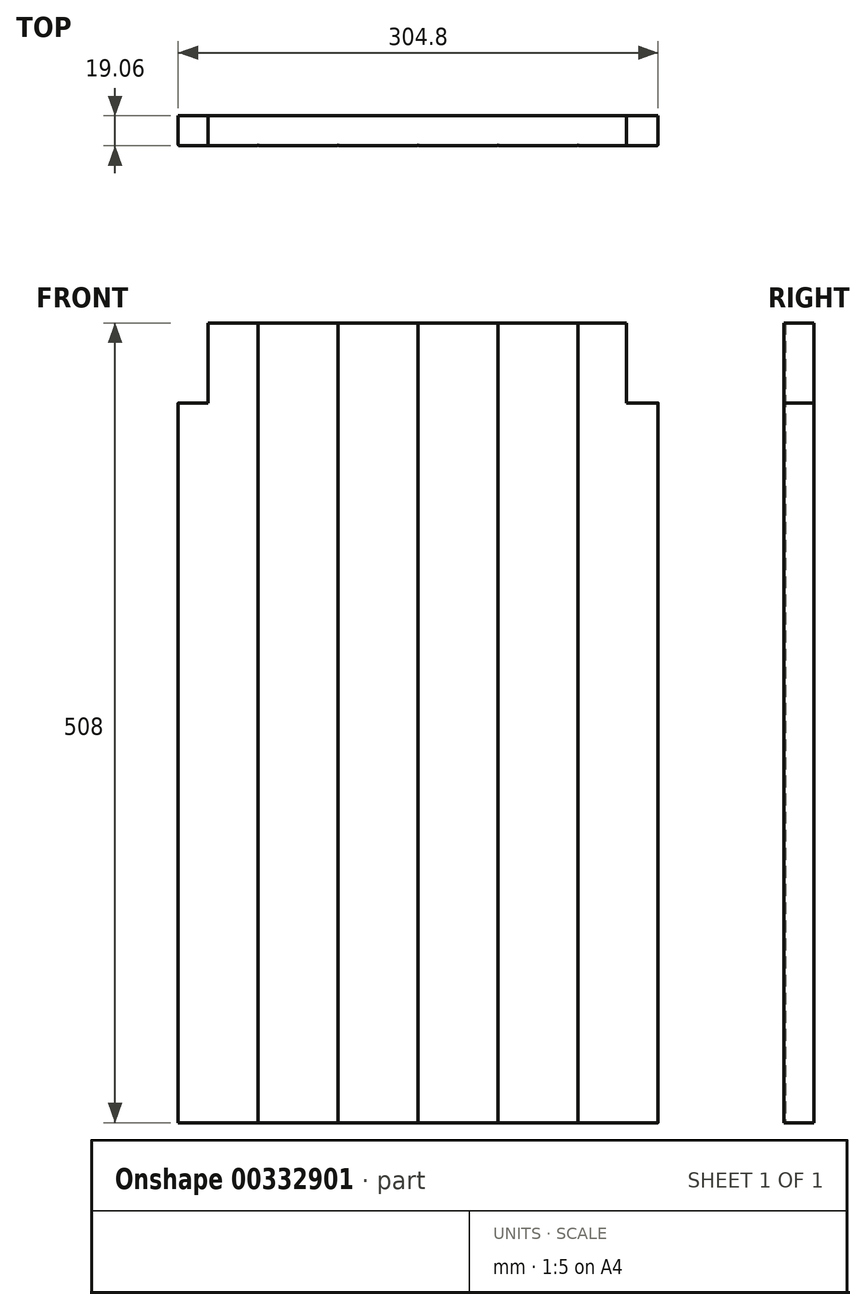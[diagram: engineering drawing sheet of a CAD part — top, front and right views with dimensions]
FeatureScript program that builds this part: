
annotation { "Feature Type Name" : "Feature", "Feature Type Description" : "" }
export const myFeature = defineFeature(function(context is Context, id is Id, definition is map)
    precondition{}
    {
        {
            var Q0;
            Q0=qCreatedBy(makeId("Top.planeOp"),FACE);
            var sketch = newSketch(context, id + "F0", { "sketchPlane" : qUnion([Q0])});
            skLineSegment(sketch, "E0.bottom", {"start": v(533.4, -9.53) * mm, "end": v(458.22, -9.53) * mm});
            skLineSegment(sketch, "E0.top", {"start": v(533.4, 9.53) * mm, "end": v(-533.4, 9.53) * mm});
            skLineSegment(sketch, "E0.left", {"start": v(533.4, 9.53) * mm, "end": v(533.4, -9.53) * mm});
            skLineSegment(sketch, "E0.right", {"start": v(-533.4, 9.53) * mm, "end": v(-533.4, -9.53) * mm});
            skPoint(sketch, "E0.middle", {"position": v(0, 0) * mm});
            skArc(sketch, "E1", {"start": v(-509.02, -9.53) * mm, "mid": v(-508.3, -9.23) * mm, "end": v(-508, -8.5) * mm});
            skArc(sketch, "E2", {"start": v(-508, -8.5) * mm, "mid": v(-507.7, -9.23) * mm, "end": v(-506.98, -9.52) * mm});
            skArc(sketch, "E3.1.0.0", {"start": v(-458.22, -9.53) * mm, "mid": v(-457.5, -9.23) * mm, "end": v(-457.2, -8.5) * mm});
            skArc(sketch, "E3.1.0.1", {"start": v(-457.2, -8.5) * mm, "mid": v(-456.9, -9.23) * mm, "end": v(-456.18, -9.52) * mm});
            skArc(sketch, "E3.2.0.0", {"start": v(-407.42, -9.53) * mm, "mid": v(-406.7, -9.23) * mm, "end": v(-406.4, -8.5) * mm});
            skArc(sketch, "E3.2.0.1", {"start": v(-406.4, -8.5) * mm, "mid": v(-406.1, -9.23) * mm, "end": v(-405.38, -9.52) * mm});
            skArc(sketch, "E3.3.0.0", {"start": v(-356.62, -9.53) * mm, "mid": v(-355.9, -9.23) * mm, "end": v(-355.6, -8.5) * mm});
            skArc(sketch, "E3.3.0.1", {"start": v(-355.6, -8.5) * mm, "mid": v(-355.3, -9.23) * mm, "end": v(-354.58, -9.52) * mm});
            skArc(sketch, "E3.4.0.0", {"start": v(-305.82, -9.53) * mm, "mid": v(-305.1, -9.23) * mm, "end": v(-304.8, -8.5) * mm});
            skArc(sketch, "E3.4.0.1", {"start": v(-304.8, -8.5) * mm, "mid": v(-304.5, -9.23) * mm, "end": v(-303.78, -9.52) * mm});
            skArc(sketch, "E3.5.0.0", {"start": v(-255.02, -9.53) * mm, "mid": v(-254.3, -9.23) * mm, "end": v(-254, -8.5) * mm});
            skArc(sketch, "E3.5.0.1", {"start": v(-254, -8.5) * mm, "mid": v(-253.7, -9.23) * mm, "end": v(-252.98, -9.52) * mm});
            skArc(sketch, "E3.6.0.0", {"start": v(-204.22, -9.53) * mm, "mid": v(-203.5, -9.23) * mm, "end": v(-203.2, -8.5) * mm});
            skArc(sketch, "E3.6.0.1", {"start": v(-203.2, -8.5) * mm, "mid": v(-202.9, -9.23) * mm, "end": v(-202.18, -9.52) * mm});
            skArc(sketch, "E3.7.0.0", {"start": v(-153.42, -9.53) * mm, "mid": v(-152.7, -9.23) * mm, "end": v(-152.4, -8.5) * mm});
            skArc(sketch, "E3.7.0.1", {"start": v(-152.4, -8.5) * mm, "mid": v(-152.1, -9.23) * mm, "end": v(-151.38, -9.52) * mm});
            skArc(sketch, "E3.8.0.0", {"start": v(-102.62, -9.53) * mm, "mid": v(-101.9, -9.23) * mm, "end": v(-101.6, -8.5) * mm});
            skArc(sketch, "E3.8.0.1", {"start": v(-101.6, -8.5) * mm, "mid": v(-101.3, -9.23) * mm, "end": v(-100.58, -9.52) * mm});
            skArc(sketch, "E3.9.0.0", {"start": v(-51.82, -9.53) * mm, "mid": v(-51.1, -9.23) * mm, "end": v(-50.8, -8.5) * mm});
            skArc(sketch, "E3.9.0.1", {"start": v(-50.8, -8.5) * mm, "mid": v(-50.5, -9.23) * mm, "end": v(-49.78, -9.52) * mm});
            skArc(sketch, "E3.10.0.0", {"start": v(-1.02, -9.53) * mm, "mid": v(-0.3, -9.23) * mm, "end": v(0, -8.5) * mm});
            skArc(sketch, "E3.10.0.1", {"start": v(0, -8.5) * mm, "mid": v(0.3, -9.23) * mm, "end": v(1.02, -9.52) * mm});
            skArc(sketch, "E3.11.0.0", {"start": v(49.78, -9.53) * mm, "mid": v(50.5, -9.23) * mm, "end": v(50.8, -8.5) * mm});
            skArc(sketch, "E3.11.0.1", {"start": v(50.8, -8.5) * mm, "mid": v(51.1, -9.23) * mm, "end": v(51.82, -9.52) * mm});
            skArc(sketch, "E3.12.0.0", {"start": v(100.58, -9.53) * mm, "mid": v(101.3, -9.23) * mm, "end": v(101.6, -8.5) * mm});
            skArc(sketch, "E3.12.0.1", {"start": v(101.6, -8.5) * mm, "mid": v(101.9, -9.23) * mm, "end": v(102.62, -9.52) * mm});
            skArc(sketch, "E3.13.0.0", {"start": v(151.38, -9.53) * mm, "mid": v(152.1, -9.23) * mm, "end": v(152.4, -8.5) * mm});
            skArc(sketch, "E3.13.0.1", {"start": v(152.4, -8.5) * mm, "mid": v(152.7, -9.23) * mm, "end": v(153.42, -9.52) * mm});
            skArc(sketch, "E3.14.0.0", {"start": v(202.18, -9.53) * mm, "mid": v(202.9, -9.23) * mm, "end": v(203.2, -8.5) * mm});
            skArc(sketch, "E3.14.0.1", {"start": v(203.2, -8.5) * mm, "mid": v(203.5, -9.23) * mm, "end": v(204.22, -9.52) * mm});
            skArc(sketch, "E3.15.0.0", {"start": v(252.98, -9.53) * mm, "mid": v(253.7, -9.23) * mm, "end": v(254, -8.5) * mm});
            skArc(sketch, "E3.15.0.1", {"start": v(254, -8.5) * mm, "mid": v(254.3, -9.23) * mm, "end": v(255.02, -9.52) * mm});
            skArc(sketch, "E3.16.0.0", {"start": v(303.78, -9.53) * mm, "mid": v(304.5, -9.23) * mm, "end": v(304.8, -8.5) * mm});
            skArc(sketch, "E3.16.0.1", {"start": v(304.8, -8.5) * mm, "mid": v(305.1, -9.23) * mm, "end": v(305.82, -9.52) * mm});
            skArc(sketch, "E3.17.0.0", {"start": v(354.58, -9.53) * mm, "mid": v(355.3, -9.23) * mm, "end": v(355.6, -8.5) * mm});
            skArc(sketch, "E3.17.0.1", {"start": v(355.6, -8.5) * mm, "mid": v(355.9, -9.23) * mm, "end": v(356.62, -9.52) * mm});
            skArc(sketch, "E3.18.0.0", {"start": v(405.38, -9.53) * mm, "mid": v(406.1, -9.23) * mm, "end": v(406.4, -8.5) * mm});
            skArc(sketch, "E3.18.0.1", {"start": v(406.4, -8.5) * mm, "mid": v(406.7, -9.23) * mm, "end": v(407.42, -9.52) * mm});
            skArc(sketch, "E3.19.0.0", {"start": v(456.18, -9.53) * mm, "mid": v(456.9, -9.23) * mm, "end": v(457.2, -8.5) * mm});
            skArc(sketch, "E3.19.0.1", {"start": v(457.2, -8.5) * mm, "mid": v(457.5, -9.23) * mm, "end": v(458.22, -9.52) * mm});
            skLineSegment(sketch, "E3.direction1", {"start": v(-506.98, -9.53) * mm, "end": v(-458.22, -9.53) * mm, "construction": true});
            skLineSegment(sketch, "E4.trimOffspring", {"start": v(-458.22, -9.53) * mm, "end": v(-533.4, -9.53) * mm});
            skLineSegment(sketch, "E5.trimOffspring", {"start": v(-407.42, -9.53) * mm, "end": v(-456.18, -9.53) * mm});
            skLineSegment(sketch, "E6.trimOffspring", {"start": v(-356.62, -9.53) * mm, "end": v(-405.38, -9.53) * mm});
            skLineSegment(sketch, "E7.trimOffspring", {"start": v(-305.82, -9.53) * mm, "end": v(-354.58, -9.53) * mm});
            skLineSegment(sketch, "E8.trimOffspring", {"start": v(-255.02, -9.53) * mm, "end": v(-303.78, -9.53) * mm});
            skLineSegment(sketch, "E9.trimOffspring", {"start": v(-204.22, -9.53) * mm, "end": v(-252.98, -9.53) * mm});
            skLineSegment(sketch, "E10.trimOffspring", {"start": v(-153.42, -9.53) * mm, "end": v(-202.18, -9.53) * mm});
            skLineSegment(sketch, "E11.trimOffspring", {"start": v(-102.62, -9.53) * mm, "end": v(-151.38, -9.53) * mm});
            skLineSegment(sketch, "E12.trimOffspring", {"start": v(-51.82, -9.53) * mm, "end": v(-100.58, -9.53) * mm});
            skLineSegment(sketch, "E13.trimOffspring", {"start": v(-1.02, -9.53) * mm, "end": v(-49.78, -9.53) * mm});
            skLineSegment(sketch, "E14.trimOffspring", {"start": v(49.78, -9.53) * mm, "end": v(1.02, -9.53) * mm});
            skLineSegment(sketch, "E15.trimOffspring", {"start": v(100.58, -9.53) * mm, "end": v(51.82, -9.53) * mm});
            skLineSegment(sketch, "E16.trimOffspring", {"start": v(151.38, -9.53) * mm, "end": v(102.62, -9.53) * mm});
            skLineSegment(sketch, "E17.trimOffspring", {"start": v(202.18, -9.53) * mm, "end": v(153.42, -9.53) * mm});
            skLineSegment(sketch, "E18.trimOffspring", {"start": v(252.98, -9.53) * mm, "end": v(204.22, -9.53) * mm});
            skLineSegment(sketch, "E19.trimOffspring", {"start": v(303.78, -9.53) * mm, "end": v(255.02, -9.53) * mm});
            skLineSegment(sketch, "E20.trimOffspring", {"start": v(354.58, -9.53) * mm, "end": v(305.82, -9.53) * mm});
            skLineSegment(sketch, "E21.trimOffspring", {"start": v(405.38, -9.53) * mm, "end": v(356.62, -9.53) * mm});
            skLineSegment(sketch, "E22.trimOffspring", {"start": v(456.18, -9.53) * mm, "end": v(407.42, -9.53) * mm});
            skSolve(sketch);
        }
        {
            var Q0;
            Q0=qSketchRegion(id+"F0",true);
            extrude(context, id + "F1", {"entities" : qUnion([Q0]), "depth" : 508 * mm});
        }
        {
            var Q0;
            Q0=qCreatedBy(makeId("Top.planeOp"),FACE);
            var sketch = newSketch(context, id + "F2", { "sketchPlane" : qUnion([Q0])});
            skLineSegment(sketch, "E23.bottom", {"start": v(-533.4, 31.1) * mm, "end": v(-152.4, 31.1) * mm});
            skLineSegment(sketch, "E23.top", {"start": v(-533.4, -50.06) * mm, "end": v(-152.4, -50.06) * mm});
            skLineSegment(sketch, "E23.left", {"start": v(-533.4, 31.1) * mm, "end": v(-533.4, -50.06) * mm});
            skLineSegment(sketch, "E23.right", {"start": v(-152.4, 31.1) * mm, "end": v(-152.4, -50.06) * mm});
            skLineSegment(sketch, "E24.bottom", {"start": v(152.4, -58.7) * mm, "end": v(533.4, -58.7) * mm});
            skLineSegment(sketch, "E24.top", {"start": v(152.4, 34.55) * mm, "end": v(533.4, 34.55) * mm});
            skLineSegment(sketch, "E24.left", {"start": v(152.4, -58.7) * mm, "end": v(152.4, 34.55) * mm});
            skLineSegment(sketch, "E24.right", {"start": v(533.4, -58.7) * mm, "end": v(533.4, 34.55) * mm});
            skSolve(sketch);
        }
        {
            var Q0;
            Q0 = qSketchRegion(id + "F2", true);
            extrude(context, id + "F3", {"entities" : qUnion([Q0]), "operationType" : NewBodyOperationType.REMOVE, "depth" : 508 * mm});
        }
        {
            var Q0;
            Q0=qCreatedBy(makeId("Front.planeOp"),FACE);
            var sketch = newSketch(context, id + "F4", { "sketchPlane" : qUnion([Q0])});
            skLineSegment(sketch, "E25.bottom", {"start": v(-238.43, 457.2) * mm, "end": v(-133.35, 457.2) * mm});
            skLineSegment(sketch, "E25.top", {"start": v(-238.43, 562.28) * mm, "end": v(-133.35, 562.28) * mm});
            skLineSegment(sketch, "E25.left", {"start": v(-238.43, 457.2) * mm, "end": v(-238.43, 562.28) * mm});
            skLineSegment(sketch, "E25.right", {"start": v(-133.35, 457.2) * mm, "end": v(-133.35, 562.28) * mm});
            skLineSegment(sketch, "E26.bottom", {"start": v(259.33, 457.2) * mm, "end": v(132.33, 457.2) * mm});
            skLineSegment(sketch, "E26.top", {"start": v(259.33, 558.8) * mm, "end": v(132.33, 558.8) * mm});
            skLineSegment(sketch, "E26.left", {"start": v(259.33, 457.2) * mm, "end": v(259.33, 558.8) * mm});
            skLineSegment(sketch, "E26.right", {"start": v(132.33, 457.2) * mm, "end": v(132.33, 558.8) * mm});
            skSolve(sketch);
        }
        {
            var Q0;
            Q0 = qSketchRegion(id + "F4", true);
            extrude(context, id + "F5", {"entities" : qUnion([Q0]), "operationType" : NewBodyOperationType.REMOVE, "endBound" : BoundingType.SYMMETRIC, "depth" : 25.4 * mm});
        }
    });
